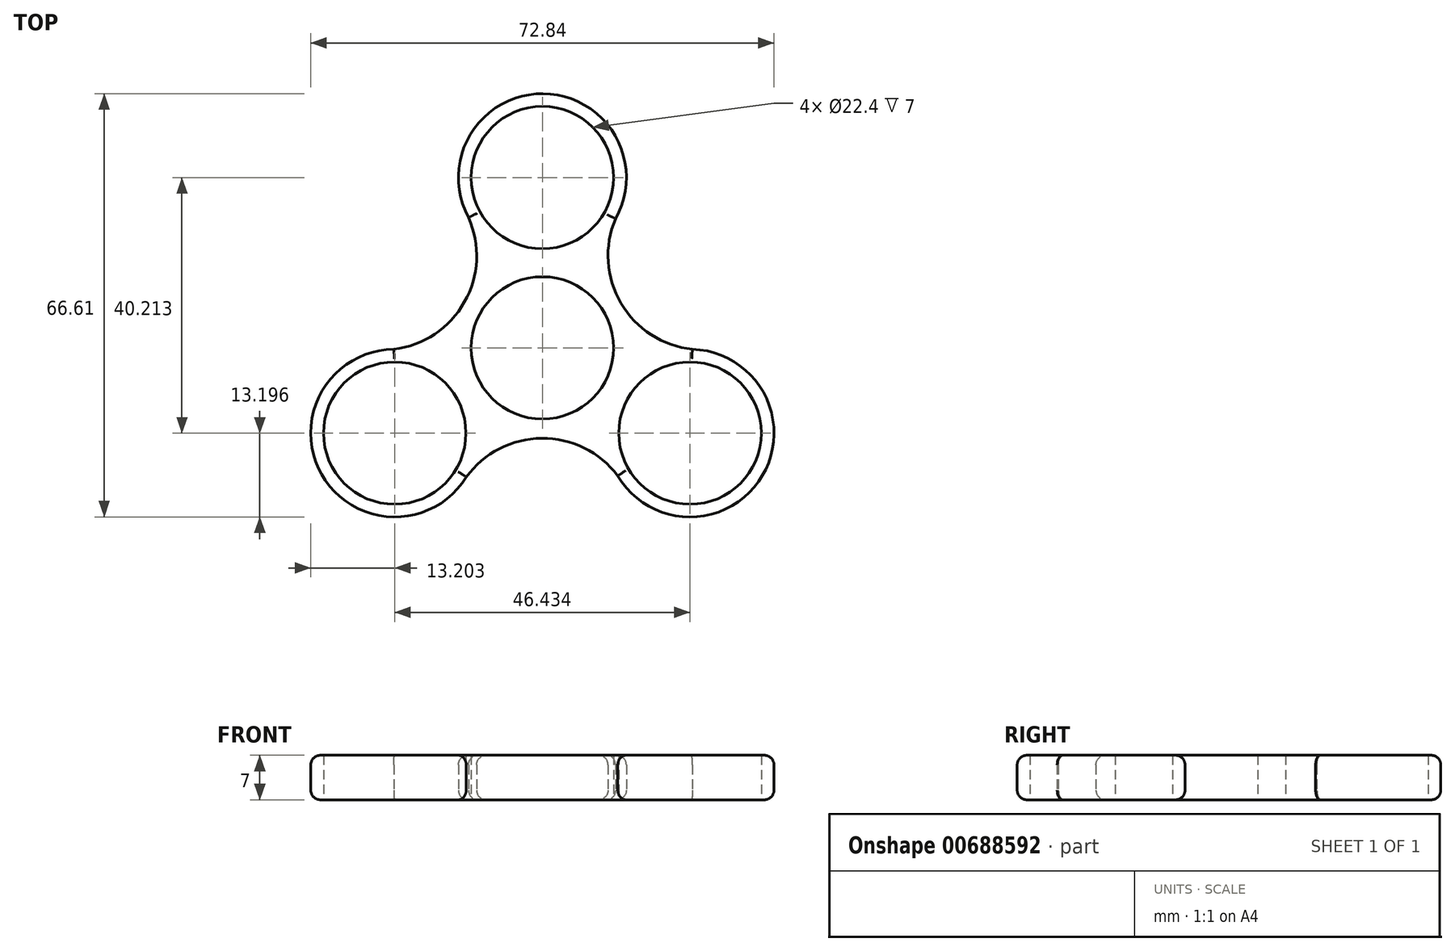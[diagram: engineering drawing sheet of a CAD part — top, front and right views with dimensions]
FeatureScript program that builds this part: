
annotation { "Feature Type Name" : "Feature", "Feature Type Description" : "" }
export const myFeature = defineFeature(function(context is Context, id is Id, definition is map)
    precondition{}
    {
        {
            var Q0;
            Q0=qCreatedBy(makeId("Top.planeOp"),FACE);
            var sketch = newSketch(context, id + "F0", { "sketchPlane" : qUnion([Q0])});
            skCircle(sketch, "E0", {"center": v(0, 0) * mm, "radius": 11.2 * mm});
            skCircle(sketch, "E1", {"center": v(0, 26.8) * mm, "radius": 11.2 * mm});
            skArc(sketch, "E2", {"start": v(11.5, 20.33) * mm, "mid": v(0.11, 40) * mm, "end": v(-11.6, 20.52) * mm});
            skArc(sketch, "E3.1.0", {"start": v(-23.35, -0.2) * mm, "mid": v(-34.7, -19.9) * mm, "end": v(-11.97, -20.31) * mm});
            skCircle(sketch, "E3.1.1", {"center": v(-23.22, -13.4) * mm, "radius": 11.2 * mm});
            skArc(sketch, "E3.2.0", {"start": v(11.85, -20.12) * mm, "mid": v(34.6, -20.1) * mm, "end": v(23.58, -0.2) * mm});
            skCircle(sketch, "E3.2.1", {"center": v(23.22, -13.4) * mm, "radius": 11.2 * mm});
            skLineSegment(sketch, "E4", {"start": v(0, 26.8) * mm, "end": v(5.6, 17.1) * mm, "construction": true});
            skArc(sketch, "E5", {"start": v(11.5, 20.33) * mm, "mid": v(12.37, 7.02) * mm, "end": v(23.58, -0.2) * mm});
            skArc(sketch, "E6.1.0", {"start": v(-23.35, -0.2) * mm, "mid": v(-12.26, 7.2) * mm, "end": v(-11.6, 20.52) * mm});
            skArc(sketch, "E6.2.0", {"start": v(11.85, -20.12) * mm, "mid": v(-0.1, -14.22) * mm, "end": v(-11.97, -20.31) * mm});
            skLineSegment(sketch, "E7.trimOffspring", {"start": v(9.7, 5.6) * mm, "end": v(12.32, 7.11) * mm, "construction": true});
            skSolve(sketch);
        }
        {
            var Q0;
            Q0=makeQuery(id+"F0.imprint","IMPRINT",FACE,{"disambiguationData":[TD([[makeQuery(id+"F0.imprint","IMPRINT",EDGE,{"derivedFrom":sQuery(id+"F0.wireOp",EDGE,"E0")}),-1.0]])]});
            extrude(context, id + "F1", {"entities" : qUnion([Q0]), "depth" : 7 * mm, "offsetDistance" : 25 * mm});
        }
        {
            var Q0;
            Q0=makeQuery(id+"F1.opExtrude","CAP_EDGE",EDGE,{"disambiguationData":[OSD([sQuery(id+"F0.wireOp",EDGE,"E6.2.0")])],"isStart":false});
            var Q1;
            Q1=makeQuery(id+"F1.opExtrude","CAP_EDGE",EDGE,{"disambiguationData":[OSD([sQuery(id+"F0.wireOp",EDGE,"E3.1.0")])],"isStart":false});
            var Q2;
            Q2=makeQuery(id+"F1.opExtrude","CAP_EDGE",EDGE,{"disambiguationData":[OSD([sQuery(id+"F0.wireOp",EDGE,"E6.1.0")])],"isStart":false});
            var Q3;
            Q3=makeQuery(id+"F1.opExtrude","CAP_EDGE",EDGE,{"disambiguationData":[OSD([sQuery(id+"F0.wireOp",EDGE,"E2")])],"isStart":false});
            var Q4;
            Q4=makeQuery(id+"F1.opExtrude","CAP_EDGE",EDGE,{"disambiguationData":[OSD([sQuery(id+"F0.wireOp",EDGE,"E5")])],"isStart":false});
            var Q5;
            Q5=makeQuery(id+"F1.opExtrude","CAP_EDGE",EDGE,{"disambiguationData":[OSD([sQuery(id+"F0.wireOp",EDGE,"E3.2.0")])],"isStart":false});
            fillet(context, id + "F2", {"entities" : qUnion([Q0, Q1, Q2, Q3, Q4, Q5]), "radius" : 1.5 * mm, "tangentPropagation" : true, "allowEdgeOverflow" : false});
        }
        {
            var Q0;
            Q0=makeQuery(id+"F1.opExtrude","CAP_EDGE",EDGE,{"disambiguationData":[OSD([sQuery(id+"F0.wireOp",EDGE,"E3.1.0")])],"isStart":true});
            var Q1;
            Q1=makeQuery(id+"F1.opExtrude","CAP_EDGE",EDGE,{"disambiguationData":[OSD([sQuery(id+"F0.wireOp",EDGE,"E6.2.0")])],"isStart":true});
            var Q2;
            Q2=makeQuery(id+"F1.opExtrude","CAP_EDGE",EDGE,{"disambiguationData":[OSD([sQuery(id+"F0.wireOp",EDGE,"E3.2.0")])],"isStart":true});
            var Q3;
            Q3=makeQuery(id+"F1.opExtrude","CAP_EDGE",EDGE,{"disambiguationData":[OSD([sQuery(id+"F0.wireOp",EDGE,"E5")])],"isStart":true});
            var Q4;
            Q4=makeQuery(id+"F1.opExtrude","CAP_EDGE",EDGE,{"disambiguationData":[OSD([sQuery(id+"F0.wireOp",EDGE,"E2")])],"isStart":true});
            var Q5;
            Q5=makeQuery(id+"F1.opExtrude","CAP_EDGE",EDGE,{"disambiguationData":[OSD([sQuery(id+"F0.wireOp",EDGE,"E6.1.0")])],"isStart":true});
            fillet(context, id + "F3", {"entities" : qUnion([Q0, Q1, Q2, Q3, Q4, Q5]), "radius" : 1.5 * mm, "tangentPropagation" : true, "allowEdgeOverflow" : false});
        }
    });
